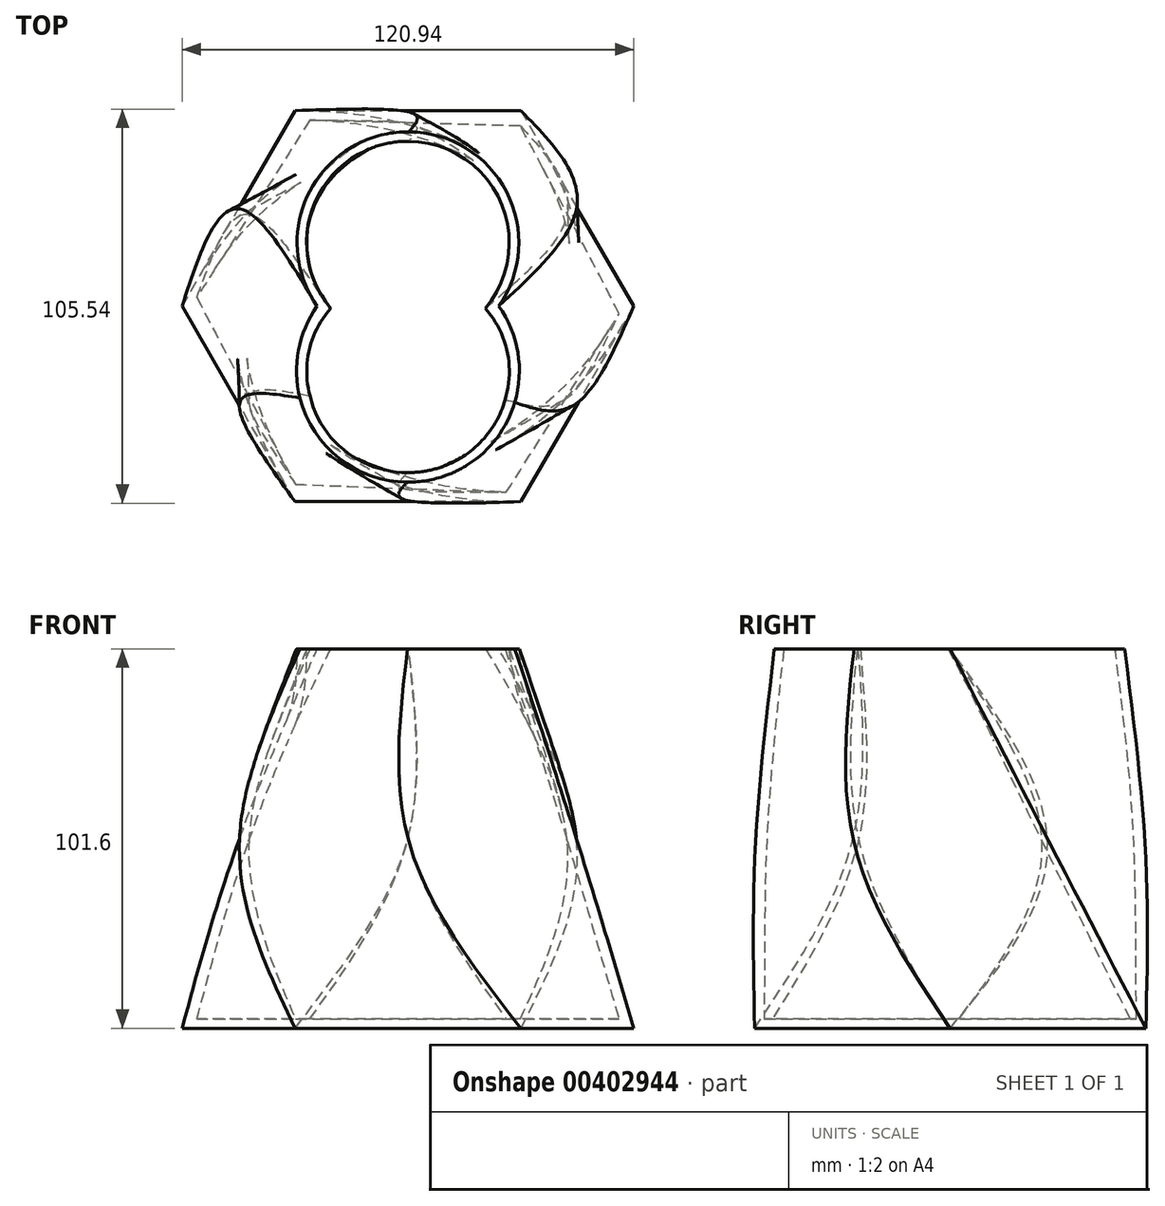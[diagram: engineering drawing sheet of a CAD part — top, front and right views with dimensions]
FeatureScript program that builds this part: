
annotation { "Feature Type Name" : "Feature", "Feature Type Description" : "" }
export const myFeature = defineFeature(function(context is Context, id is Id, definition is map)
    precondition{}
    {
        {
            var Q0;
            Q0=qCreatedBy(makeId("Top.planeOp"),FACE);
            var sketch = newSketch(context, id + "F0", { "sketchPlane" : qUnion([Q0])});
            skCircle(sketch, "E0.cCircle", {"center": v(0, 0) * mm, "radius": 52.37 * mm, "construction": true});
            skLineSegment(sketch, "E0.0", {"start": v(-30.23, 52.37) * mm, "end": v(30.23, 52.37) * mm});
            skLineSegment(sketch, "E0.1", {"start": v(30.23, 52.37) * mm, "end": v(60.47, 0) * mm});
            skLineSegment(sketch, "E0.2", {"start": v(60.47, 0) * mm, "end": v(30.23, -52.37) * mm});
            skLineSegment(sketch, "E0.3", {"start": v(30.23, -52.37) * mm, "end": v(-30.23, -52.37) * mm});
            skLineSegment(sketch, "E0.4", {"start": v(-30.23, -52.37) * mm, "end": v(-60.47, 0) * mm});
            skLineSegment(sketch, "E0.5", {"start": v(-60.47, 0) * mm, "end": v(-30.23, 52.37) * mm});
            skPoint(sketch, "E0.0.midPoint", {"position": v(0, 52.37) * mm});
            skSolve(sketch);
        }
        {
            var Q0;
            Q0=qCreatedBy(makeId("Top.planeOp"),FACE);
            cPlane(context, id + "F1", {"entities" : qUnion([Q0]), "cplaneType" : CPlaneType.OFFSET, "offset" : 50.8 * mm, "width" : 152.4 * mm, "height" : 152.4 * mm});
        }
        {
            var Q0;
            Q0=qCreatedBy(id+"F1.planeOp",FACE);
            var sketch = newSketch(context, id + "F2", { "sketchPlane" : qUnion([Q0])});
            skCircle(sketch, "E1.cCircle", {"center": v(0, 0) * mm, "radius": 45.1 * mm, "construction": true});
            skLineSegment(sketch, "E1.0", {"start": v(-45.1, -26.04) * mm, "end": v(-45.1, 26.04) * mm});
            skLineSegment(sketch, "E1.1", {"start": v(-45.1, 26.04) * mm, "end": v(0, 52.08) * mm});
            skLineSegment(sketch, "E1.2", {"start": v(0, 52.08) * mm, "end": v(45.1, 26.04) * mm});
            skLineSegment(sketch, "E1.3", {"start": v(45.1, 26.04) * mm, "end": v(45.1, -26.04) * mm});
            skLineSegment(sketch, "E1.4", {"start": v(45.1, -26.04) * mm, "end": v(0, -52.08) * mm});
            skLineSegment(sketch, "E1.5", {"start": v(0, -52.08) * mm, "end": v(-45.1, -26.04) * mm});
            skPoint(sketch, "E1.0.midPoint", {"position": v(-45.1, 0) * mm});
            skSolve(sketch);
        }
        {
            var Q0;
            Q0=qCreatedBy(id+"F1.planeOp",FACE);
            cPlane(context, id + "F3", {"entities" : qUnion([Q0]), "cplaneType" : CPlaneType.OFFSET, "offset" : 50.8 * mm, "width" : 152.4 * mm, "height" : 152.4 * mm});
        }
        {
            var Q0;
            Q0=qCreatedBy(id+"F3.planeOp",FACE);
            var sketch = newSketch(context, id + "F4", { "sketchPlane" : qUnion([Q0])});
            skArc(sketch, "E2", {"start": v(24.32, 0) * mm, "mid": v(26.36, 30.65) * mm, "end": v(0.17, 46.7) * mm});
            skArc(sketch, "E3", {"start": v(-24.32, 0) * mm, "mid": v(-29.32, -11.79) * mm, "end": v(-28.93, -24.58) * mm});
            skArc(sketch, "E4", {"start": v(0.17, 46.7) * mm, "mid": v(-26.28, 30.8) * mm, "end": v(-24.32, 0) * mm});
            skArc(sketch, "E5", {"start": v(-0.1, -47.11) * mm, "mid": v(17.81, -41.21) * mm, "end": v(28.6, -25.75) * mm});
            skArc(sketch, "E6", {"start": v(-28.93, -24.58) * mm, "mid": v(-18.37, -40.79) * mm, "end": v(-0.1, -47.11) * mm});
            skArc(sketch, "E7", {"start": v(28.6, -25.75) * mm, "mid": v(29.43, -12.38) * mm, "end": v(24.32, 0) * mm});
            skSolve(sketch);
        }
        {
            var Q0;
            Q0=makeQuery(id+"F0.imprint","IMPRINT",FACE,{"disambiguationData":[TD([[makeQuery(id+"F0.imprint","IMPRINT",EDGE,{"derivedFrom":sQuery(id+"F0.wireOp",EDGE,"E0.0")}),-1.0]])]});
            var Q1;
            Q1=makeQuery(id+"F2.imprint","IMPRINT",FACE,{"disambiguationData":[TD([[makeQuery(id+"F2.imprint","IMPRINT",EDGE,{"derivedFrom":sQuery(id+"F2.wireOp",EDGE,"E1.0")}),-1.0]])]});
            var Q2;
            Q2=makeQuery(id+"F4.imprint","IMPRINT",FACE,{"disambiguationData":[TD([[makeQuery(id+"F4.imprint","IMPRINT",EDGE,{"derivedFrom":sQuery(id+"F4.wireOp",EDGE,"E2")}),1.0]])]});
            loft(context, id + "F5", {"sheetProfilesArray" : [{ "sheetProfileEntities" : qUnion([Q0]) }, { "sheetProfileEntities" : qUnion([Q1]) }, { "sheetProfileEntities" : qUnion([Q2]) }]});
        }
        {
            var Q0;
            Q0=makeQuery(id+"F5.opLoft","CAP_FACE",FACE,{"disambiguationData":[OSD([makeQuery(id+"F4.imprint","IMPRINT",FACE,{"disambiguationData":[TD([[makeQuery(id+"F4.imprint","IMPRINT",EDGE,{"derivedFrom":sQuery(id+"F4.wireOp",EDGE,"E2")}),1.0]])]})])],"isStart":true});
            shell(context, id + "F6", {"entities" : qUnion([Q0]), "thickness" : 2.54 * mm});
        }
    });
